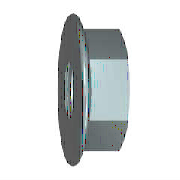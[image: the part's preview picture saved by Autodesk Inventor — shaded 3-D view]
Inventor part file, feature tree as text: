
AUTODESK INVENTOR PART (.ipt)
format: ipt  version: 2022 (Build 260153000, 153)  size: 206,336 bytes
history: native  units: mm (DEFAULTED — no unit token found)
features: sketch x3, other x2, chamfer x1, hole x1, plane x1
ambient origin geometry x7: Origin, YZ Plane, XZ Plane, X Axis, Y Axis, Z Axis, Center Point
bodies: Solid1 (feature_tree), Body (feature_tree)
feature tree (8):
  other  "Ring"
  chamfer  "Chamfer1"  Distance=10.0mm
  hole  "Thread"  [1 undecoded]
  other  "Work Axis1"
  plane  "Work Plane1"
  sketch  "Sketch1"  dims[d3=1.1mm d4=14.2mm]
  sketch  "Sketch3"  dims[d8=90.0deg]
  sketch  "Sketch4"  dims[d5=1.1mm d6=11.547005mm d7=6.0mm d9=0.0mm d10=30.0deg d11=10.0mm d24=90.0deg d25=4.917mm d26=6.0mm d27=4.0mm d28=2.0mm d29=14.3117mm d30=8.0mm d31=20.594885mm d12=0.541266mm d13=30.0deg d15=6.0mm d16=4.363323mm d45=0.0mm d46=0.541266mm d47=0.0mm d49=0.0mm d51=0.541266mm d52=2.0mm d53=45.0deg d54=0.0mm]
note: 1 required parameter value undecoded (feature->parameter linkage not recoverable at this tier; creation-order binding heuristic only, values carry confidence <= 0.55)
